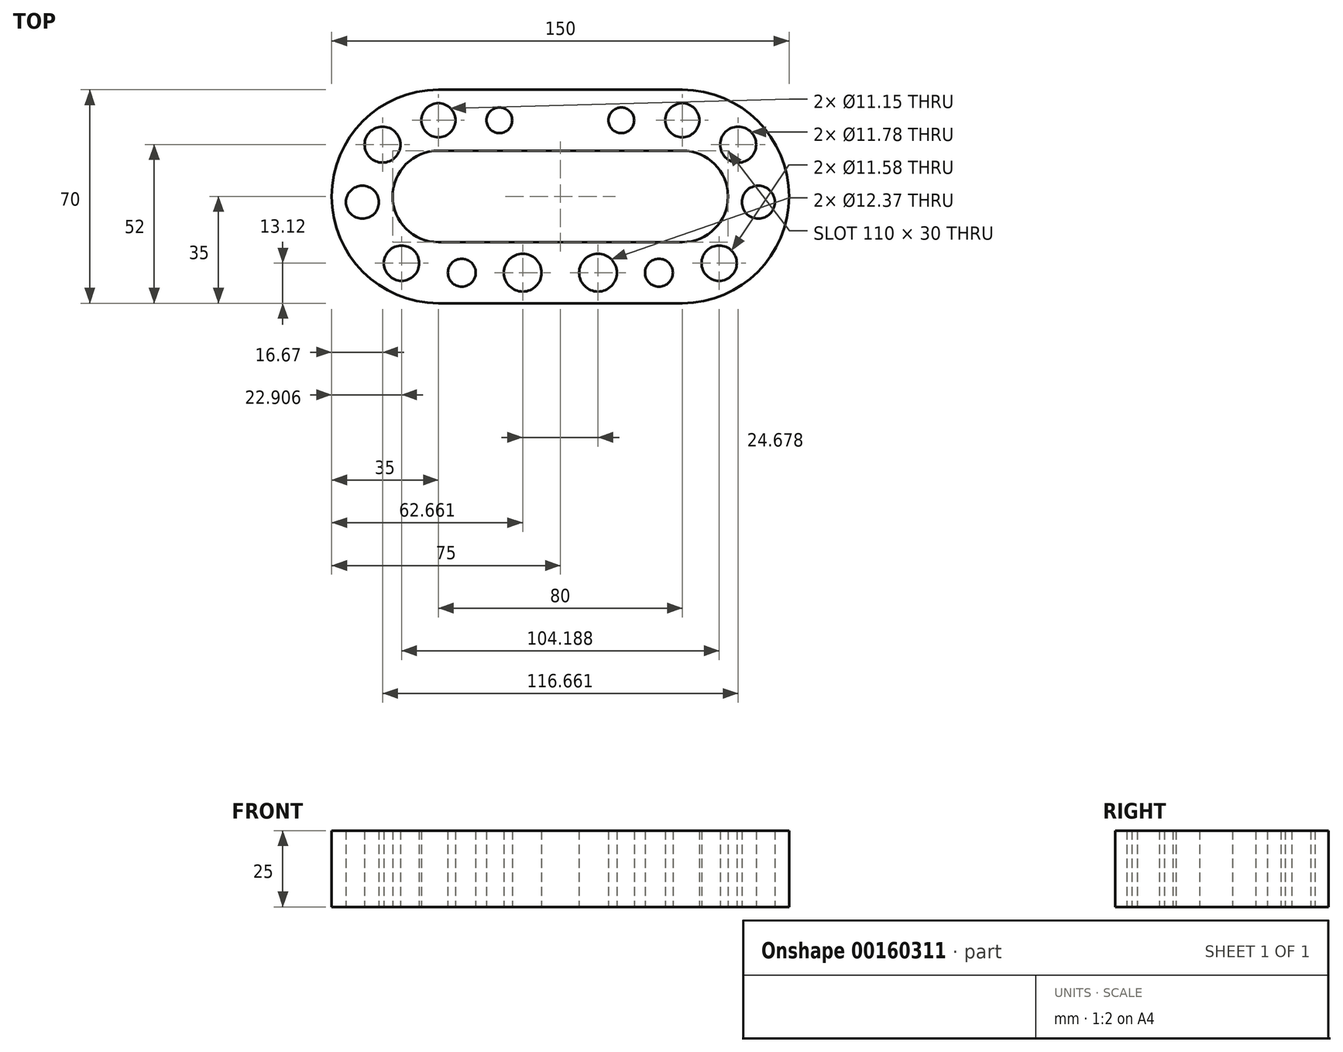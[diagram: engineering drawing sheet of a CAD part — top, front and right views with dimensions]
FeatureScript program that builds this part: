
annotation { "Feature Type Name" : "Feature", "Feature Type Description" : "" }
export const myFeature = defineFeature(function(context is Context, id is Id, definition is map)
    precondition{}
    {
        {
            var Q0;
            Q0=qCreatedBy(makeId("Top.planeOp"),FACE);
            var sketch = newSketch(context, id + "F0", { "sketchPlane" : qUnion([Q0])});
            skArc(sketch, "E0", {"start": v(-80, 15) * mm, "mid": v(-95, 0) * mm, "end": v(-80, -15) * mm});
            skArc(sketch, "E1", {"start": v(-80, 35) * mm, "mid": v(-115, 0) * mm, "end": v(-80, -35) * mm});
            skArc(sketch, "E2", {"start": v(0, -15) * mm, "mid": v(15, 0) * mm, "end": v(0, 15) * mm});
            skArc(sketch, "E3", {"start": v(0, -35) * mm, "mid": v(35, 0) * mm, "end": v(0, 35) * mm});
            skLineSegment(sketch, "E4", {"start": v(-80, 35) * mm, "end": v(0, 35) * mm});
            skLineSegment(sketch, "E5", {"start": v(-80, -35) * mm, "end": v(0, -35) * mm});
            skLineSegment(sketch, "E6", {"start": v(-80, 15) * mm, "end": v(0, 15) * mm});
            skLineSegment(sketch, "E7", {"start": v(-80, -15) * mm, "end": v(0, -15) * mm});
            skCircle(sketch, "E8", {"center": v(18.33, 17) * mm, "radius": 5.89 * mm});
            skCircle(sketch, "E9", {"center": v(24.93, -1.88) * mm, "radius": 5.4 * mm});
            skCircle(sketch, "E10", {"center": v(12.1, -21.88) * mm, "radius": 5.79 * mm});
            skCircle(sketch, "E11", {"center": v(0, 25) * mm, "radius": 5.57 * mm});
            skCircle(sketch, "E12", {"center": v(-7.66, -25) * mm, "radius": 4.57 * mm});
            skCircle(sketch, "E13", {"center": v(-20, 25) * mm, "radius": 4.21 * mm});
            skCircle(sketch, "E14", {"center": v(-27.66, -25) * mm, "radius": 6.18 * mm});
            skCircle(sketch, "E15.MirrorC", {"center": v(-52.34, -25) * mm, "radius": 6.18 * mm});
            skCircle(sketch, "E16.MirrorC", {"center": v(-72.34, -25) * mm, "radius": 4.57 * mm});
            skCircle(sketch, "E17.MirrorC", {"center": v(-92.1, -21.88) * mm, "radius": 5.79 * mm});
            skCircle(sketch, "E18.MirrorC", {"center": v(-104.93, -1.88) * mm, "radius": 5.4 * mm});
            skCircle(sketch, "E19.MirrorC", {"center": v(-98.33, 17) * mm, "radius": 5.89 * mm});
            skCircle(sketch, "E20.MirrorC", {"center": v(-80, 25) * mm, "radius": 5.57 * mm});
            skCircle(sketch, "E21.MirrorC", {"center": v(-60, 25) * mm, "radius": 4.21 * mm});
            skSolve(sketch);
        }
        {
            var Q0;
            Q0 = qSketchRegion(id + "F0", true);
            extrude(context, id + "F1", {"entities" : qUnion([Q0]), "depth" : 25 * mm});
        }
    });
